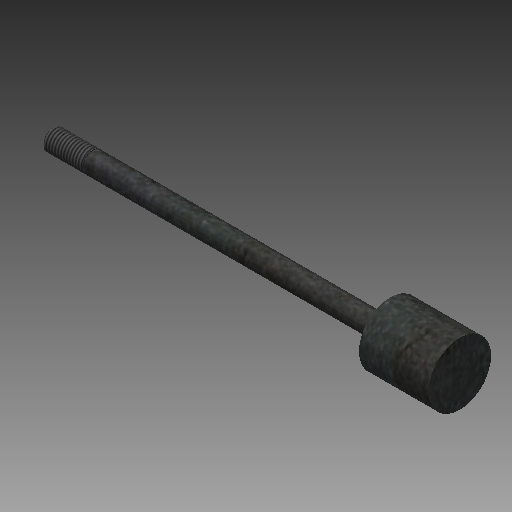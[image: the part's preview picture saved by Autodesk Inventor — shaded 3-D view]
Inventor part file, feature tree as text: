
AUTODESK INVENTOR PART (.ipt)
format: ipt  version: 2017 (Build 210142000, 142)  size: 178,176 bytes
history: native  units: in
note: dims shown in document units (in); Inventor stores cm internally (conversion verified against a paired STEP export)
features: other x70, revolve x3, sketch x3, thread x1
ambient origin geometry x8: Origin, YZ Plane, XZ Plane, XY Plane, X Axis, Y Axis, Z Axis, Center Point
bodies: Solid1 (feature_tree)
feature tree (77):
  revolve  "Revolution1"  Angle=360.0deg
  revolve  "Revolution2"  Angle=360.0deg
  thread  "Thread1"  [1 undecoded]
  revolve  "Revolution3"  [1 undecoded]
  other  "dia1_XY"
  other  "dia1_YZ"
  other  "dia1_ZX"
  other  "dia1_X"
  other  "dia1_Y"
  other  "dia1_Z"
  other  "dia1_Center"
  other  "dia12_XY"
  other  "dia12_YZ"
  other  "dia12_ZX"
  other  "dia12_X"
  other  "dia12_Y"
  other  "dia12_Z"
  other  "dia12_Center"
  other  "dia2_XY"
  other  "dia2_YZ"
  other  "dia2_ZX"
  other  "dia2_X"
  other  "dia2_Y"
  other  "dia2_Z"
  other  "dia2_Center"
  other  "dia22_XY"
  other  "dia22_YZ"
  other  "dia22_ZX"
  other  "dia22_X"
  other  "dia22_Y"
  other  "dia22_Z"
  other  "dia22_Center"
  other  "rl1_XY"
  other  "rl1_YZ"
  other  "rl1_ZX"
  other  "rl1_X"
  other  "rl1_Y"
  other  "rl1_Z"
  other  "rl1_Center"
  other  "rl2_XY"
  other  "rl2_YZ"
  other  "rl2_ZX"
  other  "rl2_X"
  other  "rl2_Y"
  other  "rl2_Z"
  other  "rl2_Center"
  other  "rod_cp_XY"
  other  "rod_cp_YZ"
  other  "rod_cp_ZX"
  other  "rod_cp_X"
  other  "rod_cp_Y"
  other  "rod_cp_Z"
  other  "rod_cp_Center"
  other  "thd1_XY"
  other  "thd1_YZ"
  other  "thd1_ZX"
  other  "thd1_X"
  other  "thd1_Y"
  other  "thd1_Z"
  other  "thd1_Center"
  other  "thd2_XY"
  other  "thd2_YZ"
  other  "thd2_ZX"
  other  "thd2_X"
  other  "thd2_Y"
  other  "thd2_Z"
  other  "thd2_Center"
  other  "to_rod_clevis_XY"
  other  "to_rod_clevis_YZ"
  other  "to_rod_clevis_ZX"
  other  "to_rod_clevis_X"
  other  "to_rod_clevis_Y"
  other  "to_rod_clevis_Z"
  other  "to_rod_clevis_Center"
  sketch  "Sketch_1"  dims[d0=360.0deg d1=360.0deg]
  sketch  "Sketch_3"  dims[d2=0.4787in d3=0.0in d4=360.0deg d5=0.0in d6=0.0in d7=0.0in]
  sketch  "Sketch_30"
note: 2 required parameter values undecoded (feature->parameter linkage not recoverable at this tier; creation-order binding heuristic only, values carry confidence <= 0.55)
